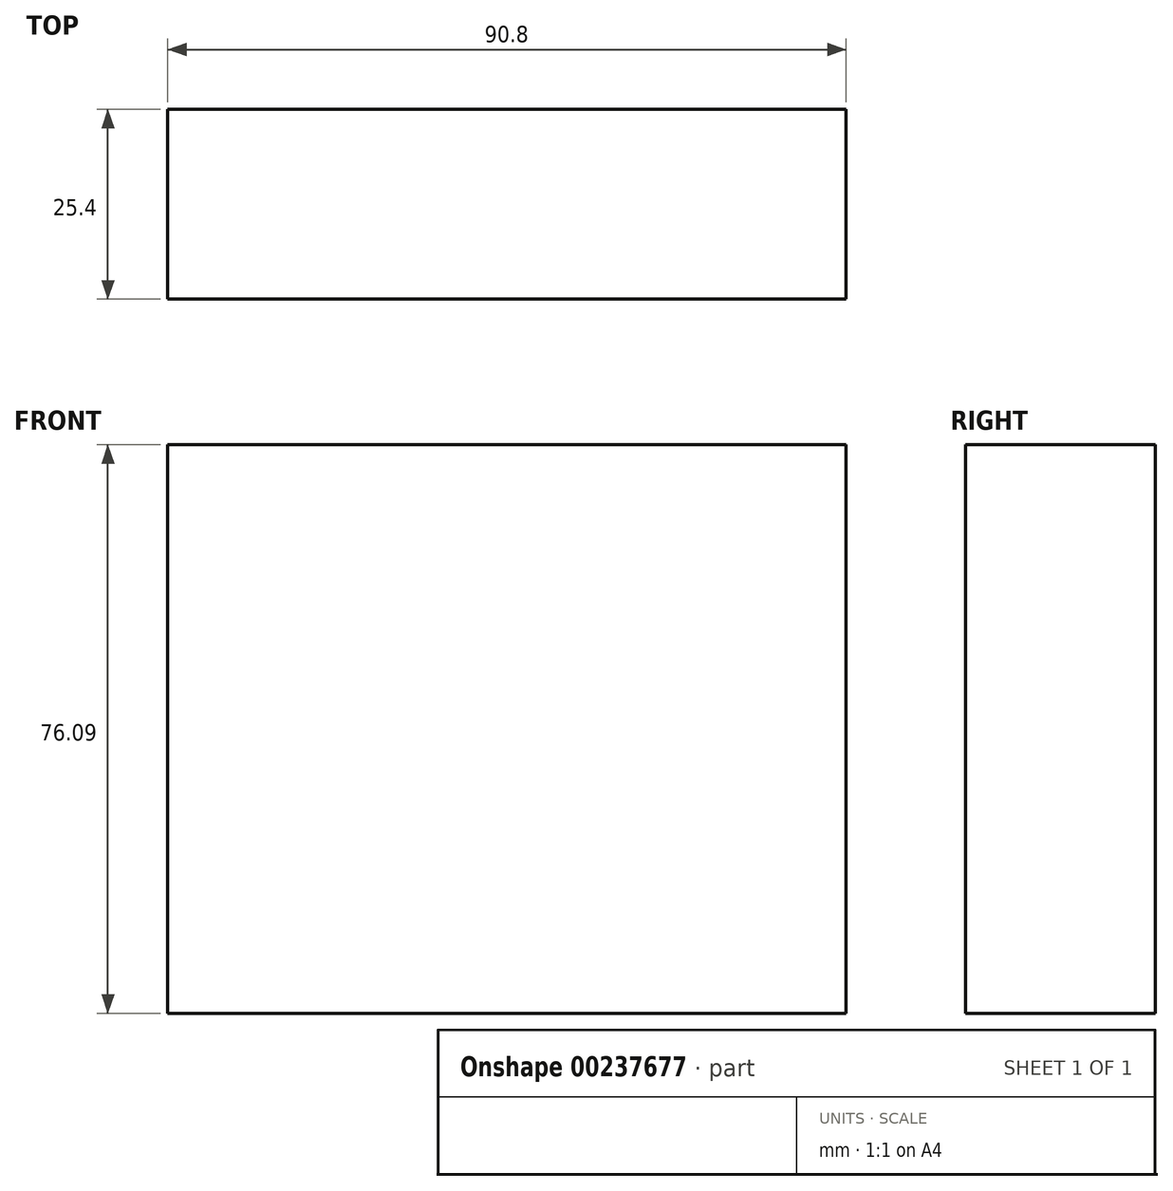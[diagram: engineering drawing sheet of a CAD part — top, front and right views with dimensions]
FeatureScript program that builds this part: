
annotation { "Feature Type Name" : "Feature", "Feature Type Description" : "" }
export const myFeature = defineFeature(function(context is Context, id is Id, definition is map)
    precondition{}
    {
        {
            var Q0;
            Q0=qCreatedBy(makeId("Front.planeOp"),FACE);
            var sketch = newSketch(context, id + "F0", { "sketchPlane" : qUnion([Q0])});
            skLineSegment(sketch, "E0.bottom", {"start": v(-4.98, 0) * mm, "end": v(-95.78, 0) * mm});
            skLineSegment(sketch, "E0.top", {"start": v(-4.98, -76.1) * mm, "end": v(-95.78, -76.1) * mm});
            skLineSegment(sketch, "E0.left", {"start": v(-4.98, 0) * mm, "end": v(-4.98, -76.1) * mm});
            skLineSegment(sketch, "E0.right", {"start": v(-95.78, 0) * mm, "end": v(-95.78, -76.1) * mm});
            skSolve(sketch);
        }
        {
            var Q0;
            Q0 = qSketchRegion(id + "F0", true);
            extrude(context, id + "F1", {"entities" : qUnion([Q0]), "depth" : 25.4 * mm});
        }
    });
